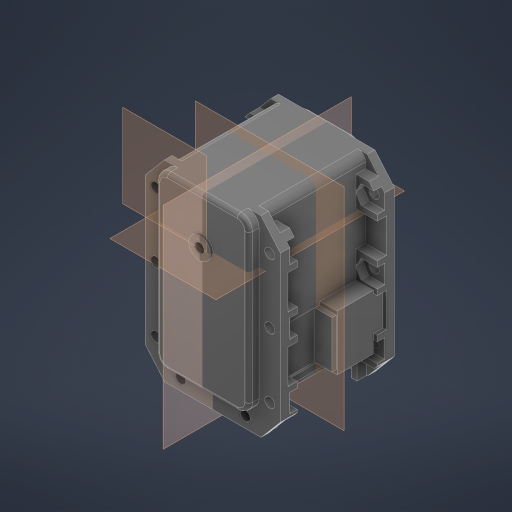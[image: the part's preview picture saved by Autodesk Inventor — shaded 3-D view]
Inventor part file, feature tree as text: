
AUTODESK INVENTOR PART (.ipt)
format: ipt  version: 2024 (Build 280153000, 153)  size: 650,240 bytes
history: native  units: mm
features: other x7, extrude x6, projected_geometry x5, sketch x3
ambient origin geometry x8: Origin, YZ Plane, XZ Plane, XY Plane, X Axis, Y Axis, Z Axis, Center Point
bodies: Body1 (feature_tree)
feature tree (21):
  other  "솔리드1"
  other  "작업 평면7"
  extrude  "돌출1"  Depth=22.0mm
  extrude  "돌출2"  Depth=2.0mm TaperAngle=0.0deg
  extrude  "돌출3"  Depth=8.0mm
  extrude  "돌출4"  Depth=0.75mm TaperAngle=0.0deg
  other  "작업 평면5"
  other  "작업 평면6"
  other  "작업 평면8"
  extrude  "돌출5"  Depth=4.5mm
  extrude  "돌출6"  Depth=2.5mm TaperAngle=0.0deg
  other  "스레드1"
  projected_geometry  "투영된 루프1"
  projected_geometry  "투영된 루프2"
  sketch  "스케치4"
  projected_geometry  "투영된 루프3"
  sketch  "스케치5"
  projected_geometry  "투영된 루프4"
  sketch  "스케치6"
  projected_geometry  "투영된 루프5"
  other  "기준1"
